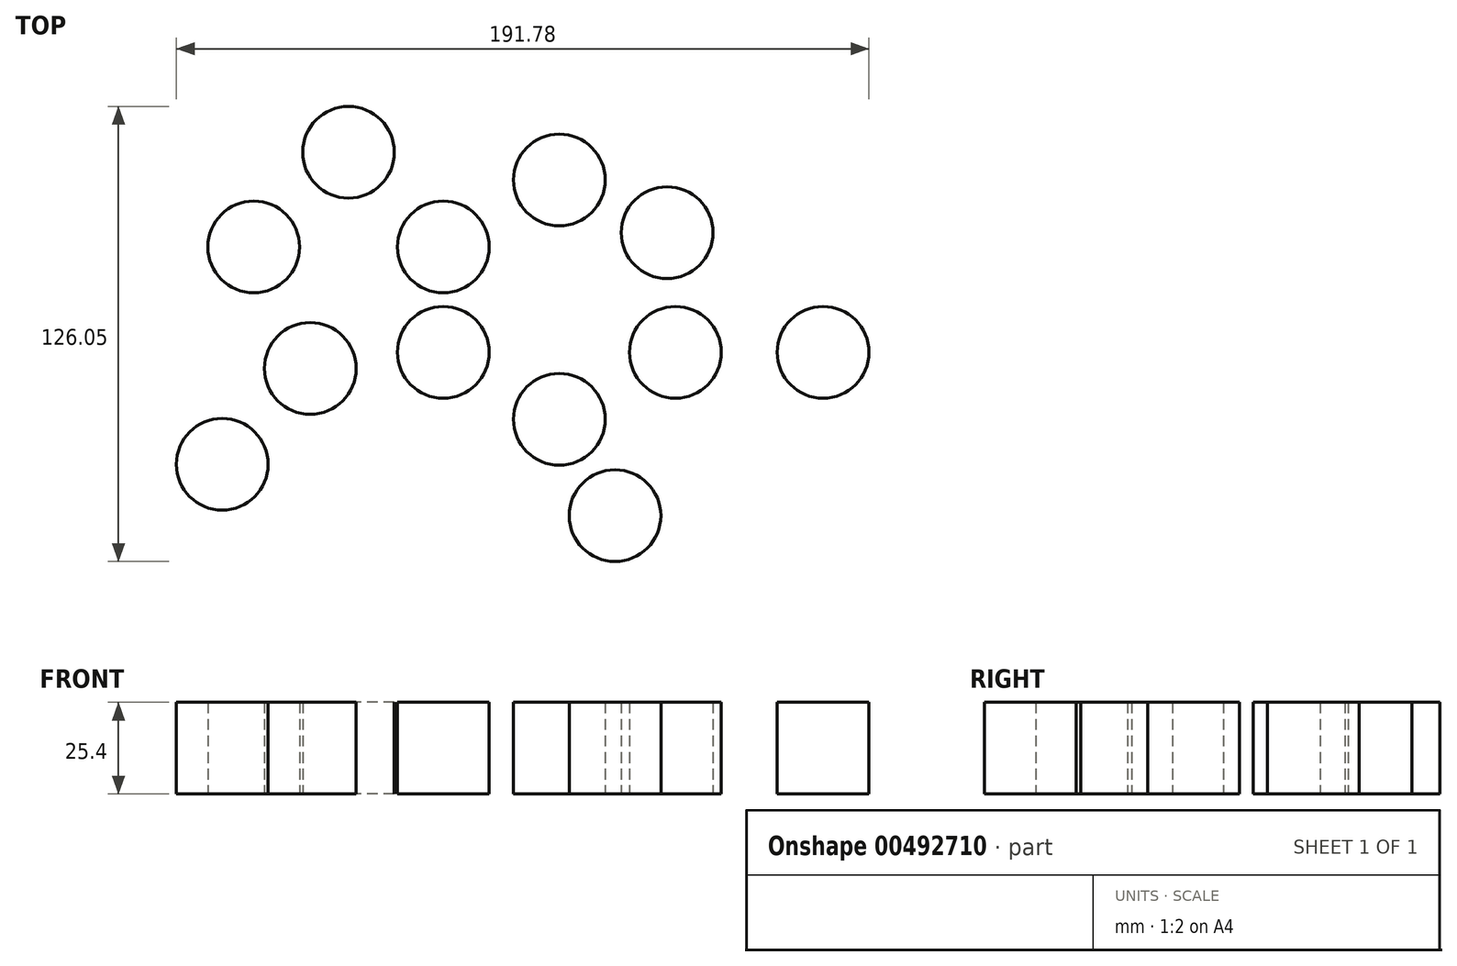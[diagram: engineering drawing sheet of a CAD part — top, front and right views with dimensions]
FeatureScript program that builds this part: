
annotation { "Feature Type Name" : "Feature", "Feature Type Description" : "" }
export const myFeature = defineFeature(function(context is Context, id is Id, definition is map)
    precondition{}
    {
        {
            var Q0;
            Q0=qCreatedBy(makeId("Top.planeOp"),FACE);
            var sketch = newSketch(context, id + "F0", { "sketchPlane" : qUnion([Q0])});
            skCircle(sketch, "E0", {"center": v(0, 0) * mm, "radius": 12.7 * mm});
            skLineSegment(sketch, "E1", {"start": v(0, 0) * mm, "end": v(32.14, 18.56) * mm});
            skCircle(sketch, "E2", {"center": v(32.14, 18.56) * mm, "radius": 12.7 * mm});
            skCircle(sketch, "E3", {"center": v(-26.24, 26.24) * mm, "radius": 12.7 * mm});
            skLineSegment(sketch, "E4", {"start": v(-26.24, 26.24) * mm, "end": v(-52.48, 0) * mm});
            skCircle(sketch, "E5", {"center": v(-52.48, 0) * mm, "radius": 12.7 * mm});
            skLineSegment(sketch, "E6", {"start": v(-52.48, 0) * mm, "end": v(-36.84, -33.65) * mm});
            skCircle(sketch, "E7", {"center": v(-36.84, -33.65) * mm, "radius": 12.7 * mm});
            skLineSegment(sketch, "E8", {"start": v(-36.84, -33.65) * mm, "end": v(0, -29.18) * mm});
            skCircle(sketch, "E9", {"center": v(0, -29.18) * mm, "radius": 12.7 * mm});
            skLineSegment(sketch, "E10", {"start": v(0, -29.18) * mm, "end": v(32.14, -47.73) * mm});
            skCircle(sketch, "E11", {"center": v(32.14, -47.73) * mm, "radius": 12.7 * mm});
            skCircle(sketch, "E12", {"center": v(64.28, -29.18) * mm, "radius": 12.7 * mm});
            skLineSegment(sketch, "E13", {"start": v(0, -29.18) * mm, "end": v(0, 0) * mm});
            skLineSegment(sketch, "E14", {"start": v(32.14, -47.73) * mm, "end": v(64.28, -29.18) * mm});
            skLineSegment(sketch, "E15", {"start": v(64.28, -29.18) * mm, "end": v(61.99, 3.97) * mm});
            skCircle(sketch, "E16", {"center": v(61.99, 3.97) * mm, "radius": 12.7 * mm});
            skLineSegment(sketch, "E17", {"start": v(61.99, 3.97) * mm, "end": v(32.14, 18.56) * mm});
            skLineSegment(sketch, "E18", {"start": v(-36.84, -33.65) * mm, "end": v(-61.21, -60.19) * mm});
            skCircle(sketch, "E19", {"center": v(-61.21, -60.19) * mm, "radius": 12.7 * mm});
            skLineSegment(sketch, "E20", {"start": v(32.14, -47.73) * mm, "end": v(47.54, -74.41) * mm});
            skCircle(sketch, "E21", {"center": v(47.54, -74.41) * mm, "radius": 12.7 * mm});
            skLineSegment(sketch, "E22", {"start": v(64.28, -29.18) * mm, "end": v(105.17, -29.18) * mm});
            skLineSegment(sketch, "E23", {"start": v(0, 0) * mm, "end": v(-26.24, 26.24) * mm});
            skCircle(sketch, "E24", {"center": v(105.17, -29.18) * mm, "radius": 12.7 * mm});
            skSolve(sketch);
        }
        {
            var Q0;
            {var subQ0=sQuery(id+"F0.wireOp",EDGE,"E6");var subQ1=sQuery(id+"F0.wireOp",EDGE,"E4");var subQ2=makeQuery(id+"F0.imprint","INTERSECT",VERTEX,{"derivedFrom":[subQ1,subQ0]});Q0=makeQuery(id+"F0.imprint","IMPRINT",FACE,{"disambiguationData":[TD([[makeQuery(id+"F0.imprint","IMPRINT",EDGE,{"disambiguationData":[TD([[subQ2,1.0]])],"derivedFrom":subQ1}),-1.0]])]});}
            var Q1;
            {var subQ0=sQuery(id+"F0.wireOp",EDGE,"E6");var subQ1=sQuery(id+"F0.wireOp",EDGE,"E4");var subQ2=makeQuery(id+"F0.imprint","INTERSECT",VERTEX,{"derivedFrom":[subQ1,subQ0]});Q1=makeQuery(id+"F0.imprint","IMPRINT",FACE,{"disambiguationData":[TD([[makeQuery(id+"F0.imprint","IMPRINT",EDGE,{"disambiguationData":[TD([[subQ2,1.0]])],"derivedFrom":subQ1}),1.0]])]});}
            var Q2;
            {var subQ0=sQuery(id+"F0.wireOp",EDGE,"E4");var subQ1=sQuery(id+"F0.wireOp",EDGE,"E3");var subQ2=makeQuery(id+"F0.imprint","INTERSECT",VERTEX,{"derivedFrom":[subQ1,subQ0]});Q2=makeQuery(id+"F0.imprint","IMPRINT",FACE,{"disambiguationData":[TD([[makeQuery(id+"F0.imprint","IMPRINT",EDGE,{"disambiguationData":[TD([[subQ2,1.0]])],"derivedFrom":subQ1}),1.0]])]});}
            var Q3;
            {var subQ0=sQuery(id+"F0.wireOp",EDGE,"E4");var subQ1=sQuery(id+"F0.wireOp",EDGE,"E3");var subQ2=makeQuery(id+"F0.imprint","INTERSECT",VERTEX,{"derivedFrom":[subQ1,subQ0]});Q3=makeQuery(id+"F0.imprint","IMPRINT",FACE,{"disambiguationData":[TD([[makeQuery(id+"F0.imprint","IMPRINT",EDGE,{"disambiguationData":[TD([[subQ2,-1.0]])],"derivedFrom":subQ1}),1.0]])]});}
            var Q4;
            {var subQ0=sQuery(id+"F0.wireOp",EDGE,"E23");var subQ1=sQuery(id+"F0.wireOp",EDGE,"E0");var subQ2=makeQuery(id+"F0.imprint","INTERSECT",VERTEX,{"derivedFrom":[subQ1,subQ0]});Q4=makeQuery(id+"F0.imprint","IMPRINT",FACE,{"disambiguationData":[TD([[makeQuery(id+"F0.imprint","IMPRINT",EDGE,{"disambiguationData":[TD([[subQ2,-1.0]])],"derivedFrom":subQ1}),1.0]])]});}
            var Q5;
            {var subQ0=sQuery(id+"F0.wireOp",EDGE,"E1");var subQ1=sQuery(id+"F0.wireOp",EDGE,"E0");var subQ2=makeQuery(id+"F0.imprint","INTERSECT",VERTEX,{"derivedFrom":[subQ1,subQ0]});Q5=makeQuery(id+"F0.imprint","IMPRINT",FACE,{"disambiguationData":[TD([[makeQuery(id+"F0.imprint","IMPRINT",EDGE,{"disambiguationData":[TD([[subQ2,-1.0]])],"derivedFrom":subQ1}),1.0]])]});}
            var Q6;
            {var subQ0=sQuery(id+"F0.wireOp",EDGE,"E1");var subQ1=sQuery(id+"F0.wireOp",EDGE,"E0");var subQ2=makeQuery(id+"F0.imprint","INTERSECT",VERTEX,{"derivedFrom":[subQ1,subQ0]});Q6=makeQuery(id+"F0.imprint","IMPRINT",FACE,{"disambiguationData":[TD([[makeQuery(id+"F0.imprint","IMPRINT",EDGE,{"disambiguationData":[TD([[subQ2,1.0]])],"derivedFrom":subQ1}),1.0]])]});}
            var Q7;
            {var subQ1=sQuery(id+"F0.wireOp",EDGE,"E8");var subQ3=sQuery(id+"F0.wireOp",EDGE,"E9");var subQ4=makeQuery(id+"F0.imprint","INTERSECT",VERTEX,{"derivedFrom":[subQ1,subQ3]});Q7=makeQuery(id+"F0.imprint","IMPRINT",FACE,{"disambiguationData":[TD([[makeQuery(id+"F0.imprint","IMPRINT",EDGE,{"disambiguationData":[TD([[subQ4,1.0]])],"derivedFrom":subQ3}),1.0]])]});}
            var Q8;
            {var subQ0=sQuery(id+"F0.wireOp",EDGE,"E18");var subQ1=sQuery(id+"F0.wireOp",EDGE,"E7");var subQ2=makeQuery(id+"F0.imprint","INTERSECT",VERTEX,{"derivedFrom":[subQ1,subQ0]});Q8=makeQuery(id+"F0.imprint","IMPRINT",FACE,{"disambiguationData":[TD([[makeQuery(id+"F0.imprint","IMPRINT",EDGE,{"disambiguationData":[TD([[subQ2,-1.0]])],"derivedFrom":subQ1}),1.0]])]});}
            var Q9;
            {var subQ1=sQuery(id+"F0.wireOp",EDGE,"E6");var subQ3=sQuery(id+"F0.wireOp",EDGE,"E7");var subQ4=makeQuery(id+"F0.imprint","INTERSECT",VERTEX,{"derivedFrom":[subQ1,subQ3]});Q9=makeQuery(id+"F0.imprint","IMPRINT",FACE,{"disambiguationData":[TD([[makeQuery(id+"F0.imprint","IMPRINT",EDGE,{"disambiguationData":[TD([[subQ4,1.0]])],"derivedFrom":subQ3}),1.0]])]});}
            var Q10;
            Q10=makeQuery(id+"F0.imprint","IMPRINT",FACE,{"disambiguationData":[TD([[makeQuery(id+"F0.imprint","IMPRINT",EDGE,{"derivedFrom":sQuery(id+"F0.wireOp",EDGE,"E19")}),1.0]])]});
            var Q11;
            {var subQ0=sQuery(id+"F0.wireOp",EDGE,"E18");var subQ3=sQuery(id+"F0.wireOp",EDGE,"E7");var subQ5=makeQuery(id+"F0.imprint","INTERSECT",VERTEX,{"derivedFrom":[subQ3,subQ0]});Q11=makeQuery(id+"F0.imprint","IMPRINT",FACE,{"disambiguationData":[TD([[makeQuery(id+"F0.imprint","IMPRINT",EDGE,{"disambiguationData":[TD([[subQ5,1.0]])],"derivedFrom":subQ3}),1.0]])]});}
            var Q12;
            {var subQ1=sQuery(id+"F0.wireOp",EDGE,"E8");var subQ3=sQuery(id+"F0.wireOp",EDGE,"E9");var subQ4=makeQuery(id+"F0.imprint","INTERSECT",VERTEX,{"derivedFrom":[subQ1,subQ3]});Q12=makeQuery(id+"F0.imprint","IMPRINT",FACE,{"disambiguationData":[TD([[makeQuery(id+"F0.imprint","IMPRINT",EDGE,{"disambiguationData":[TD([[subQ4,-1.0]])],"derivedFrom":subQ3}),1.0]])]});}
            var Q13;
            {var subQ0=sQuery(id+"F0.wireOp",EDGE,"E10");var subQ1=sQuery(id+"F0.wireOp",EDGE,"E9");var subQ2=makeQuery(id+"F0.imprint","INTERSECT",VERTEX,{"derivedFrom":[subQ1,subQ0]});Q13=makeQuery(id+"F0.imprint","IMPRINT",FACE,{"disambiguationData":[TD([[makeQuery(id+"F0.imprint","IMPRINT",EDGE,{"disambiguationData":[TD([[subQ2,-1.0]])],"derivedFrom":subQ1}),1.0]])]});}
            var Q14;
            {var subQ1=sQuery(id+"F0.wireOp",EDGE,"E10");var subQ3=sQuery(id+"F0.wireOp",EDGE,"E11");var subQ4=makeQuery(id+"F0.imprint","INTERSECT",VERTEX,{"derivedFrom":[subQ1,subQ3]});Q14=makeQuery(id+"F0.imprint","IMPRINT",FACE,{"disambiguationData":[TD([[makeQuery(id+"F0.imprint","IMPRINT",EDGE,{"disambiguationData":[TD([[subQ4,1.0]])],"derivedFrom":subQ3}),1.0]])]});}
            var Q15;
            {var subQ0=sQuery(id+"F0.wireOp",EDGE,"E20");var subQ3=sQuery(id+"F0.wireOp",EDGE,"E11");var subQ5=makeQuery(id+"F0.imprint","INTERSECT",VERTEX,{"derivedFrom":[subQ3,subQ0]});Q15=makeQuery(id+"F0.imprint","IMPRINT",FACE,{"disambiguationData":[TD([[makeQuery(id+"F0.imprint","IMPRINT",EDGE,{"disambiguationData":[TD([[subQ5,1.0]])],"derivedFrom":subQ3}),1.0]])]});}
            var Q16;
            {var subQ0=sQuery(id+"F0.wireOp",EDGE,"E20");var subQ1=sQuery(id+"F0.wireOp",EDGE,"E11");var subQ2=makeQuery(id+"F0.imprint","INTERSECT",VERTEX,{"derivedFrom":[subQ1,subQ0]});Q16=makeQuery(id+"F0.imprint","IMPRINT",FACE,{"disambiguationData":[TD([[makeQuery(id+"F0.imprint","IMPRINT",EDGE,{"disambiguationData":[TD([[subQ2,-1.0]])],"derivedFrom":subQ1}),1.0]])]});}
            var Q17;
            Q17=makeQuery(id+"F0.imprint","IMPRINT",FACE,{"disambiguationData":[TD([[makeQuery(id+"F0.imprint","IMPRINT",EDGE,{"derivedFrom":sQuery(id+"F0.wireOp",EDGE,"E21")}),1.0]])]});
            var Q18;
            {var subQ0=sQuery(id+"F0.wireOp",EDGE,"E22");var subQ1=sQuery(id+"F0.wireOp",EDGE,"E12");var subQ2=makeQuery(id+"F0.imprint","INTERSECT",VERTEX,{"derivedFrom":[subQ1,subQ0]});Q18=makeQuery(id+"F0.imprint","IMPRINT",FACE,{"disambiguationData":[TD([[makeQuery(id+"F0.imprint","IMPRINT",EDGE,{"disambiguationData":[TD([[subQ2,1.0]])],"derivedFrom":subQ1}),1.0]])]});}
            var Q19;
            {var subQ0=sQuery(id+"F0.wireOp",EDGE,"E15");var subQ1=sQuery(id+"F0.wireOp",EDGE,"E12");var subQ2=makeQuery(id+"F0.imprint","INTERSECT",VERTEX,{"derivedFrom":[subQ1,subQ0]});Q19=makeQuery(id+"F0.imprint","IMPRINT",FACE,{"disambiguationData":[TD([[makeQuery(id+"F0.imprint","IMPRINT",EDGE,{"disambiguationData":[TD([[subQ2,-1.0]])],"derivedFrom":subQ1}),1.0]])]});}
            var Q20;
            {var subQ0=sQuery(id+"F0.wireOp",EDGE,"E22");var subQ1=sQuery(id+"F0.wireOp",EDGE,"E12");var subQ2=makeQuery(id+"F0.imprint","INTERSECT",VERTEX,{"derivedFrom":[subQ1,subQ0]});Q20=makeQuery(id+"F0.imprint","IMPRINT",FACE,{"disambiguationData":[TD([[makeQuery(id+"F0.imprint","IMPRINT",EDGE,{"disambiguationData":[TD([[subQ2,-1.0]])],"derivedFrom":subQ1}),1.0]])]});}
            var Q21;
            Q21=makeQuery(id+"F0.imprint","IMPRINT",FACE,{"disambiguationData":[TD([[makeQuery(id+"F0.imprint","IMPRINT",EDGE,{"derivedFrom":sQuery(id+"F0.wireOp",EDGE,"E24")}),1.0]])]});
            var Q22;
            {var subQ0=sQuery(id+"F0.wireOp",EDGE,"E17");var subQ1=sQuery(id+"F0.wireOp",EDGE,"E15");var subQ2=makeQuery(id+"F0.imprint","INTERSECT",VERTEX,{"derivedFrom":[subQ1,subQ0]});Q22=makeQuery(id+"F0.imprint","IMPRINT",FACE,{"disambiguationData":[TD([[makeQuery(id+"F0.imprint","IMPRINT",EDGE,{"disambiguationData":[TD([[subQ2,1.0]])],"derivedFrom":subQ1}),-1.0]])]});}
            var Q23;
            {var subQ0=sQuery(id+"F0.wireOp",EDGE,"E17");var subQ1=sQuery(id+"F0.wireOp",EDGE,"E15");var subQ2=makeQuery(id+"F0.imprint","INTERSECT",VERTEX,{"derivedFrom":[subQ1,subQ0]});Q23=makeQuery(id+"F0.imprint","IMPRINT",FACE,{"disambiguationData":[TD([[makeQuery(id+"F0.imprint","IMPRINT",EDGE,{"disambiguationData":[TD([[subQ2,1.0]])],"derivedFrom":subQ1}),1.0]])]});}
            var Q24;
            {var subQ0=sQuery(id+"F0.wireOp",EDGE,"E17");var subQ1=sQuery(id+"F0.wireOp",EDGE,"E1");var subQ2=makeQuery(id+"F0.imprint","INTERSECT",VERTEX,{"derivedFrom":[subQ1,subQ0]});Q24=makeQuery(id+"F0.imprint","IMPRINT",FACE,{"disambiguationData":[TD([[makeQuery(id+"F0.imprint","IMPRINT",EDGE,{"disambiguationData":[TD([[subQ2,1.0]])],"derivedFrom":subQ1}),-1.0]])]});}
            var Q25;
            {var subQ0=sQuery(id+"F0.wireOp",EDGE,"E17");var subQ1=sQuery(id+"F0.wireOp",EDGE,"E1");var subQ2=makeQuery(id+"F0.imprint","INTERSECT",VERTEX,{"derivedFrom":[subQ1,subQ0]});Q25=makeQuery(id+"F0.imprint","IMPRINT",FACE,{"disambiguationData":[TD([[makeQuery(id+"F0.imprint","IMPRINT",EDGE,{"disambiguationData":[TD([[subQ2,1.0]])],"derivedFrom":subQ1}),1.0]])]});}
            extrude(context, id + "F1", {"entities" : qUnion([Q0, Q1, Q2, Q3, Q4, Q5, Q6, Q7, Q8, Q9, Q10, Q11, Q12, Q13, Q14, Q15, Q16, Q17, Q18, Q19, Q20, Q21, Q22, Q23, Q24, Q25]), "depth" : 25.4 * mm});
        }
    });
